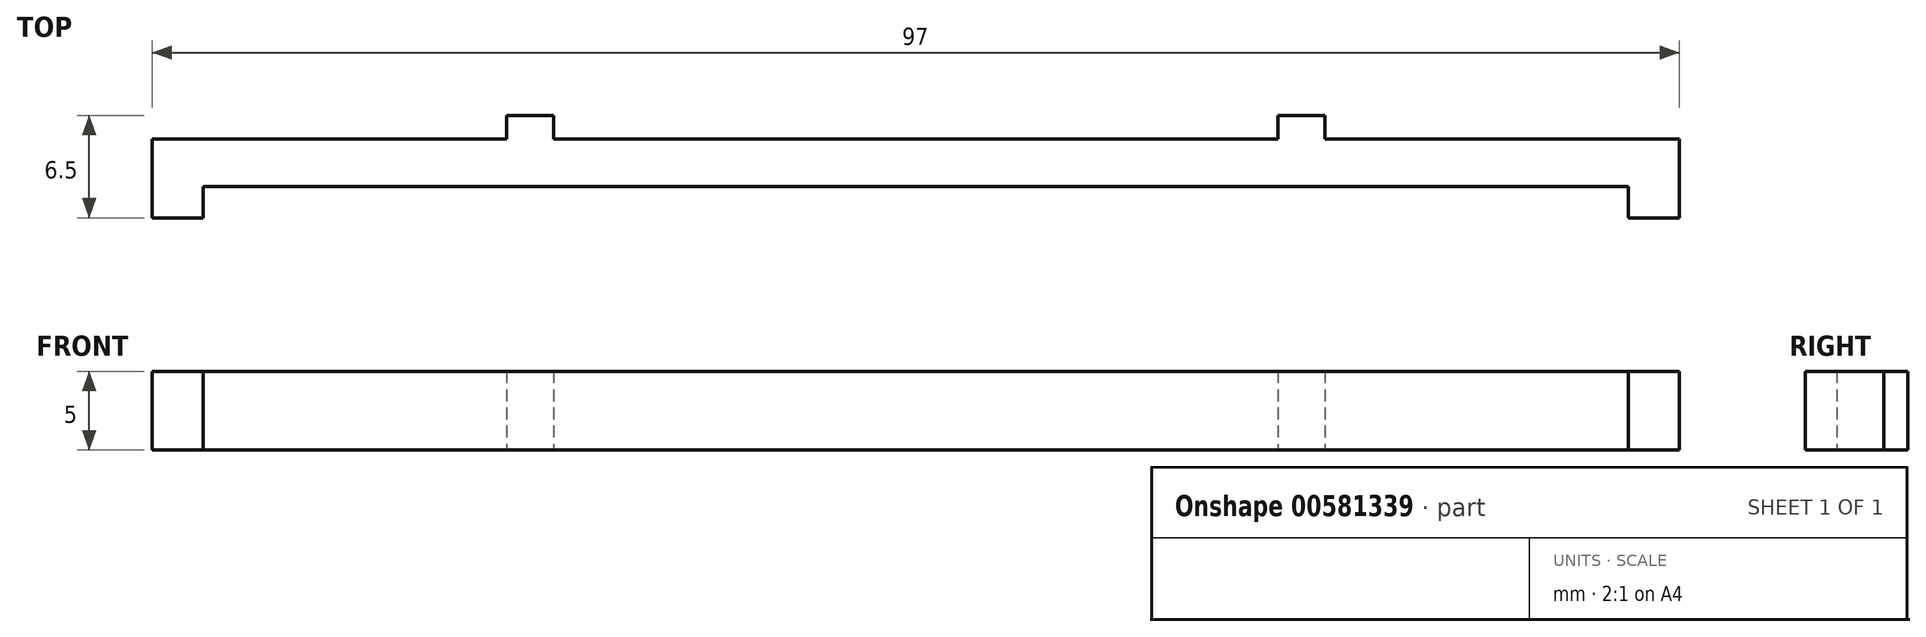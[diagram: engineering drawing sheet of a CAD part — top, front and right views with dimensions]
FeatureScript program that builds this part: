
annotation { "Feature Type Name" : "Feature", "Feature Type Description" : "" }
export const myFeature = defineFeature(function(context is Context, id is Id, definition is map)
    precondition{}
    {
        {
            var Q0;
            Q0=qCreatedBy(makeId("Top.planeOp"),FACE);
            var sketch = newSketch(context, id + "F0", { "sketchPlane" : qUnion([Q0])});
            skLineSegment(sketch, "E0.bottom", {"start": v(45.25, -1.5) * mm, "end": v(-45.25, -1.5) * mm});
            skLineSegment(sketch, "E0.top", {"start": v(45.25, 1.5) * mm, "end": v(-45.25, 1.5) * mm});
            skLineSegment(sketch, "E0.left", {"start": v(45.25, -1.5) * mm, "end": v(45.25, 1.5) * mm});
            skLineSegment(sketch, "E0.right", {"start": v(-45.25, -1.5) * mm, "end": v(-45.25, 1.5) * mm});
            skPoint(sketch, "E0.middle", {"position": v(0, 0) * mm});
            skLineSegment(sketch, "E1.bottom", {"start": v(-45.25, 1.5) * mm, "end": v(-48.5, 1.5) * mm});
            skLineSegment(sketch, "E1.top", {"start": v(-45.25, -3.5) * mm, "end": v(-48.5, -3.5) * mm});
            skLineSegment(sketch, "E1.left", {"start": v(-45.25, 1.5) * mm, "end": v(-45.25, -3.5) * mm});
            skLineSegment(sketch, "E1.right", {"start": v(-48.5, 1.5) * mm, "end": v(-48.5, -3.5) * mm});
            skLineSegment(sketch, "E2.bottom", {"start": v(45.25, 1.5) * mm, "end": v(48.5, 1.5) * mm});
            skLineSegment(sketch, "E2.top", {"start": v(45.25, -3.5) * mm, "end": v(48.5, -3.5) * mm});
            skLineSegment(sketch, "E2.left", {"start": v(45.25, 1.5) * mm, "end": v(45.25, -3.5) * mm});
            skLineSegment(sketch, "E2.right", {"start": v(48.5, 1.5) * mm, "end": v(48.5, -3.5) * mm});
            skLineSegment(sketch, "E3.bottom", {"start": v(-48.5, 1.5) * mm, "end": v(48.5, 1.5) * mm, "construction": true});
            skLineSegment(sketch, "E3.top", {"start": v(-48.5, 12.97) * mm, "end": v(48.5, 12.97) * mm, "construction": true});
            skLineSegment(sketch, "E3.left", {"start": v(-48.5, 1.5) * mm, "end": v(-48.5, 12.97) * mm, "construction": true});
            skLineSegment(sketch, "E3.right", {"start": v(48.5, 1.5) * mm, "end": v(48.5, 12.97) * mm, "construction": true});
            skLineSegment(sketch, "E4.bottom", {"start": v(-48.5, 12.97) * mm, "end": v(-23, 12.97) * mm, "construction": true});
            skLineSegment(sketch, "E4.top", {"start": v(-48.5, 1.5) * mm, "end": v(-23, 1.5) * mm, "construction": true});
            skLineSegment(sketch, "E4.left", {"start": v(-48.5, 12.97) * mm, "end": v(-48.5, 1.5) * mm, "construction": true});
            skLineSegment(sketch, "E4.right", {"start": v(-23, 12.97) * mm, "end": v(-23, 1.5) * mm, "construction": true});
            skLineSegment(sketch, "E5.bottom", {"start": v(48.5, 12.97) * mm, "end": v(23, 12.97) * mm, "construction": true});
            skLineSegment(sketch, "E5.top", {"start": v(48.5, 1.5) * mm, "end": v(23, 1.5) * mm, "construction": true});
            skLineSegment(sketch, "E5.left", {"start": v(48.5, 12.97) * mm, "end": v(48.5, 1.5) * mm, "construction": true});
            skLineSegment(sketch, "E5.right", {"start": v(23, 12.97) * mm, "end": v(23, 1.5) * mm, "construction": true});
            skLineSegment(sketch, "E6.bottom", {"start": v(-23, 1.5) * mm, "end": v(-26, 1.5) * mm});
            skLineSegment(sketch, "E6.top", {"start": v(-23, 3) * mm, "end": v(-26, 3) * mm});
            skLineSegment(sketch, "E6.left", {"start": v(-23, 1.5) * mm, "end": v(-23, 3) * mm});
            skLineSegment(sketch, "E6.right", {"start": v(-26, 1.5) * mm, "end": v(-26, 3) * mm});
            skLineSegment(sketch, "E7.bottom", {"start": v(23, 1.5) * mm, "end": v(26, 1.5) * mm});
            skLineSegment(sketch, "E7.top", {"start": v(23, 3) * mm, "end": v(26, 3) * mm});
            skLineSegment(sketch, "E7.left", {"start": v(23, 1.5) * mm, "end": v(23, 3) * mm});
            skLineSegment(sketch, "E7.right", {"start": v(26, 1.5) * mm, "end": v(26, 3) * mm});
            skSolve(sketch);
        }
        {
            var Q0;
            {var subQ1=sQuery(id+"F0.wireOp",EDGE,"E0.left");var subQ2=makeQuery(id+"F0.imprint","IMPRINT",EDGE,{"derivedFrom":subQ1});var subQ10=sQuery(id+"F0.wireOp",EDGE,"E0.right");var subQ16=makeQuery(id+"F0.imprint","IMPRINT",EDGE,{"derivedFrom":subQ10});Q0=qUnion([makeQuery(id+"F0.imprint","IMPRINT",FACE,{"disambiguationData":[TD([[subQ16,1.0]])]}),makeQuery(id+"F0.imprint","IMPRINT",FACE,{"disambiguationData":[TD([[makeQuery(id+"F0.imprint","IMPRINT",EDGE,{"derivedFrom":sQuery(id+"F0.wireOp",EDGE,"E6.top")}),1.0]])]}),makeQuery(id+"F0.imprint","IMPRINT",FACE,{"disambiguationData":[TD([[makeQuery(id+"F0.imprint","IMPRINT",EDGE,{"derivedFrom":sQuery(id+"F0.wireOp",EDGE,"E0.bottom")}),-1.0]])]}),makeQuery(id+"F0.imprint","IMPRINT",FACE,{"disambiguationData":[TD([[makeQuery(id+"F0.imprint","IMPRINT",EDGE,{"derivedFrom":sQuery(id+"F0.wireOp",EDGE,"E7.top")}),-1.0]])]}),makeQuery(id+"F0.imprint","IMPRINT",FACE,{"disambiguationData":[TD([[subQ2,-1.0]])]})]);}
            extrude(context, id + "F1", {"entities" : qUnion([Q0]), "depth" : 5 * mm, "offsetDistance" : 25 * mm});
        }
    });
